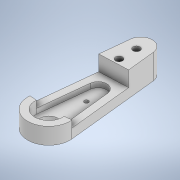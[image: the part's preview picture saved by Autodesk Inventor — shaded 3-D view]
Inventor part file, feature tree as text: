
AUTODESK INVENTOR PART (.ipt)
format: ipt  version: 2020.3 (Build 243373000, 373)  size: 160,256 bytes
history: native  units: mm
features: extrude x4, sketch x1
ambient origin geometry x8: Origin, YZ Plane, XZ Plane, XY Plane, X Axis, Y Axis, Z Axis, Center Point
bodies: Solid1 (feature_tree)
feature tree (5):
  sketch  "Sketch1"  dims[d2=2.0mm d3=2.0mm d4=1.2mm d5=5.0mm d6=12.043mm d7=8.009mm d8=6.548mm d9=5.009mm d10=5.0mm d11=1.226mm d12=6.0mm d15=26.302mm d16=3.34mm d17=10.66mm d18=26.302mm d19=25.0mm d20=4.7mm d21=0.0mm d22=2.7mm d23=0.0mm d24=1.2mm d25=0.0mm d26=7.1mm d27=0.0mm d28=0.5mm]
  extrude  "Extrusion1"  Depth=2.0mm
  extrude  "Extrusion2"  Depth=1.2mm
  extrude  "Extrusion3"  Depth=0.5mm
  extrude  "Extrusion4"  Depth=0.5mm
